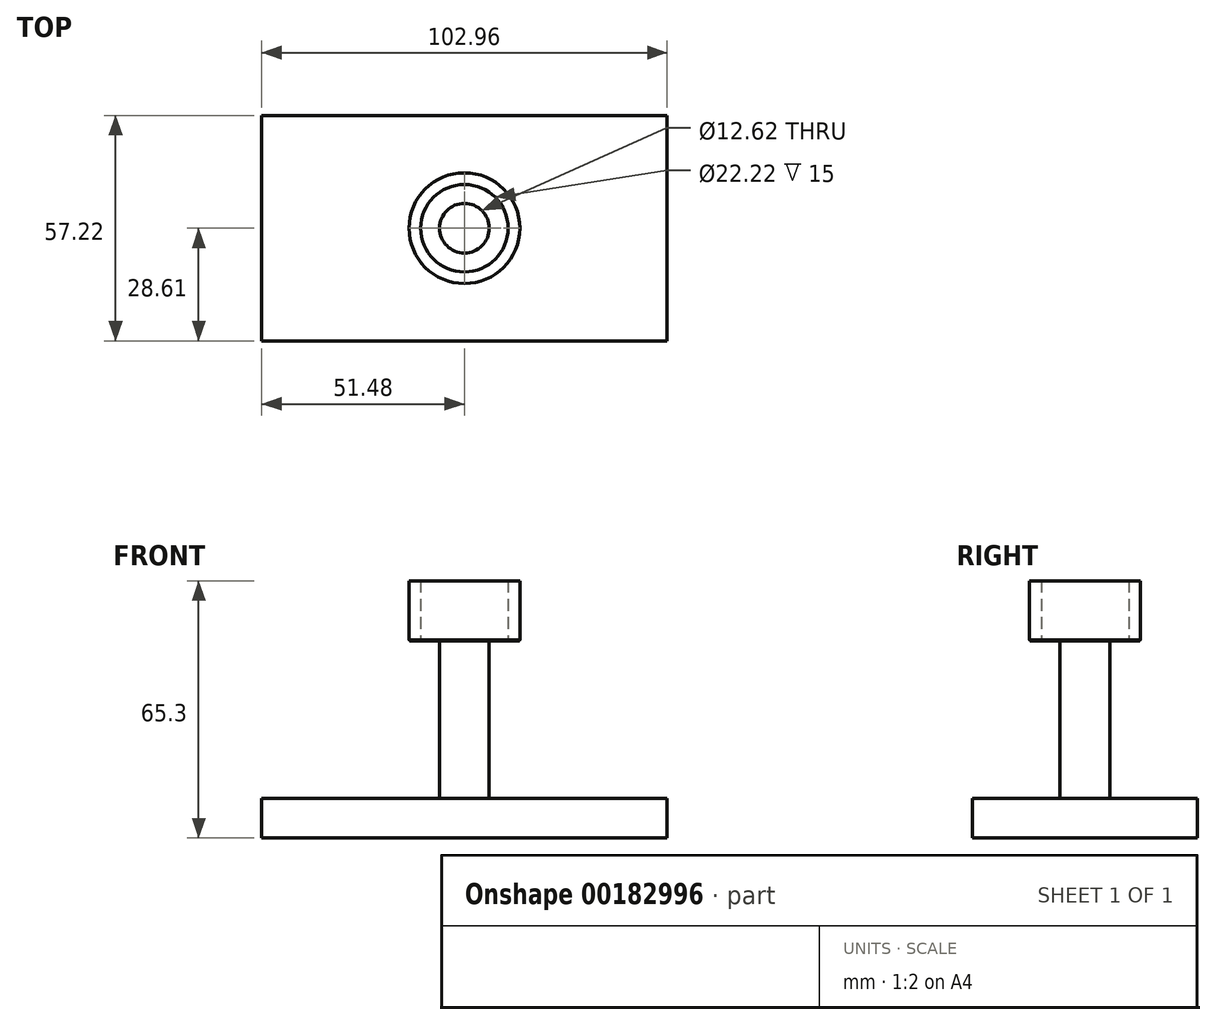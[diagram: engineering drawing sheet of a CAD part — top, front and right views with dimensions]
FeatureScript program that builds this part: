
annotation { "Feature Type Name" : "Feature", "Feature Type Description" : "" }
export const myFeature = defineFeature(function(context is Context, id is Id, definition is map)
    precondition{}
    {
        {
            var Q0;
            Q0=qCreatedBy(makeId("Top.planeOp"),FACE);
            var sketch = newSketch(context, id + "F0", { "sketchPlane" : qUnion([Q0])});
            skLineSegment(sketch, "E0.bottom", {"start": v(51.48, -28.61) * mm, "end": v(-51.48, -28.61) * mm});
            skLineSegment(sketch, "E0.top", {"start": v(51.48, 28.61) * mm, "end": v(-51.48, 28.61) * mm});
            skLineSegment(sketch, "E0.left", {"start": v(51.48, -28.61) * mm, "end": v(51.48, 28.61) * mm});
            skLineSegment(sketch, "E0.right", {"start": v(-51.48, -28.61) * mm, "end": v(-51.48, 28.61) * mm});
            skPoint(sketch, "E0.middle", {"position": v(0, 0) * mm});
            skSolve(sketch);
        }
        {
            var Q0;
            Q0=makeQuery(id+"F0.imprint","IMPRINT",FACE,{"disambiguationData":[TD([[makeQuery(id+"F0.imprint","IMPRINT",EDGE,{"derivedFrom":sQuery(id+"F0.wireOp",EDGE,"E0.bottom")}),-1.0]])]});
            extrude(context, id + "F1", {"entities" : qUnion([Q0]), "depth" : 10 * mm});
        }
        {
            var Q0;
            Q0=makeQuery(id+"F1.opExtrude","CAP_FACE",FACE,{"disambiguationData":[OSD([sQuery(id+"F0.wireOp",EDGE,"E0.bottom"),sQuery(id+"F0.wireOp",EDGE,"E0.top"),sQuery(id+"F0.wireOp",EDGE,"E0.left"),sQuery(id+"F0.wireOp",EDGE,"E0.right")])],"isStart":false});
            var sketch = newSketch(context, id + "F2", { "sketchPlane" : qUnion([Q0])});
            skCircle(sketch, "E1", {"center": v(0, 0) * mm, "radius": 6.31 * mm});
            skSolve(sketch);
        }
        {
            var Q0;
            Q0=makeQuery(id+"F2.imprint","IMPRINT",FACE,{"disambiguationData":[TD([[makeQuery(id+"F2.imprint","IMPRINT",EDGE,{"derivedFrom":sQuery(id+"F2.wireOp",EDGE,"E1")}),1.0]])]});
            extrude(context, id + "F3", {"entities" : qUnion([Q0]), "operationType" : NewBodyOperationType.ADD, "depth" : 40.3 * mm});
        }
        {
            var Q0;
            Q0=makeQuery(id+"F3.opExtrude","CAP_FACE",FACE,{"disambiguationData":[OSD([sQuery(id+"F2.wireOp",EDGE,"E1")])],"isStart":false});
            var sketch = newSketch(context, id + "F4", { "sketchPlane" : qUnion([Q0])});
            skCircle(sketch, "E2", {"center": v(0, 0) * mm, "radius": 14.07 * mm});
            skCircle(sketch, "E3", {"center": v(0, 0) * mm, "radius": 11.1 * mm});
            skSolve(sketch);
        }
        {
            var Q0;
            Q0=makeQuery(id+"F4.imprint","IMPRINT",FACE,{"disambiguationData":[TD([[makeQuery(id+"F4.imprint","IMPRINT",EDGE,{"derivedFrom":sQuery(id+"F4.wireOp",EDGE,"E2")}),1.0]])]});
            extrude(context, id + "F5", {"entities" : qUnion([Q0]), "depth" : 15 * mm});
        }
        {
            var Q0;
            Q0=makeQuery(id+"F3.opExtrude","CAP_FACE",FACE,{"disambiguationData":[OSD([sQuery(id+"F2.wireOp",EDGE,"E1")])],"isStart":false});
            var sketch = newSketch(context, id + "F6", { "sketchPlane" : qUnion([Q0])});
            skCircle(sketch, "E4", {"center": v(0, 0) * mm, "radius": 14 * mm});
            skSolve(sketch);
        }
        {
            var Q0;
            Q0=makeQuery(id+"F6.imprint","IMPRINT",FACE,{"disambiguationData":[TD([[makeQuery(id+"F6.imprint","IMPRINT",EDGE,{"derivedFrom":sQuery(id+"F6.wireOp",EDGE,"E4")}),1.0]])]});
            extrude(context, id + "F7", {"entities" : qUnion([Q0]), "oppositeDirection" : true, "depth" : 0.3 * mm});
        }
    });
